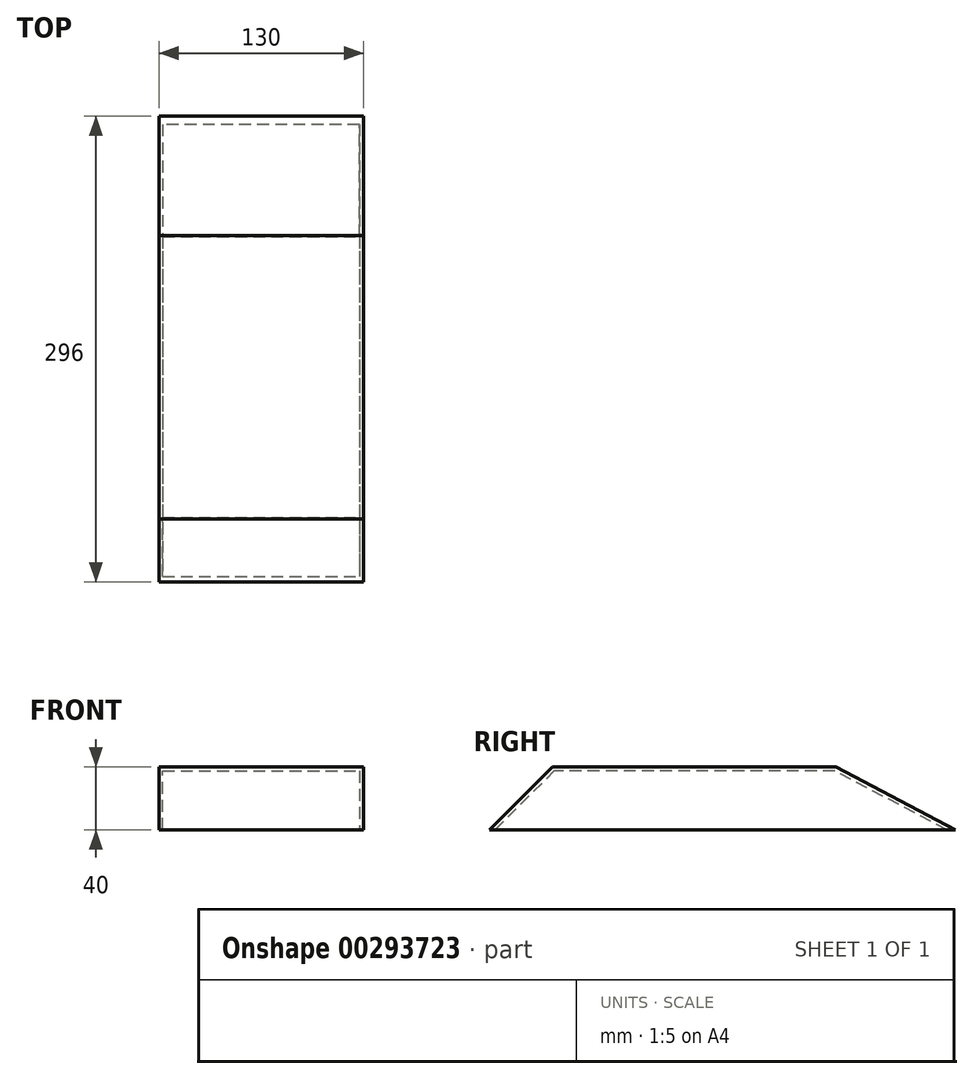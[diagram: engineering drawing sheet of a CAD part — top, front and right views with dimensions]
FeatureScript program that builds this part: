
annotation { "Feature Type Name" : "Feature", "Feature Type Description" : "" }
export const myFeature = defineFeature(function(context is Context, id is Id, definition is map)
    precondition{}
    {
        {
            var Q0;
            Q0=qCreatedBy(makeId("Top.planeOp"),FACE);
            var sketch = newSketch(context, id + "F0", { "sketchPlane" : qUnion([Q0])});
            skLineSegment(sketch, "E0.bottom", {"start": v(-65, 148) * mm, "end": v(65, 148) * mm});
            skLineSegment(sketch, "E0.top", {"start": v(-65, -148) * mm, "end": v(65, -148) * mm});
            skLineSegment(sketch, "E0.left", {"start": v(-65, 148) * mm, "end": v(-65, -148) * mm});
            skLineSegment(sketch, "E0.right", {"start": v(65, 148) * mm, "end": v(65, -148) * mm});
            skPoint(sketch, "E0.middle", {"position": v(0, 0) * mm});
            skSolve(sketch);
        }
        {
            var Q0;
            Q0 = qSketchRegion(id + "F0", true);
            extrude(context, id + "F1", {"entities" : qUnion([Q0]), "endBound" : BoundingType.SYMMETRIC, "depth" : 40 * mm});
        }
        {
            var Q0;
            Q0=makeQuery(id+"F1.opExtrude","CAP_EDGE",EDGE,{"disambiguationData":[OSD([sQuery(id+"F0.wireOp",EDGE,"E0.bottom")])],"isStart":false});
            chamfer(context, id + "F2", {"entities" : qUnion([Q0]), "chamferType" : ChamferType.TWO_OFFSETS, "width1" : 40 * mm, "oppositeDirection" : false, "width2" : 76 * mm, "tangentPropagation" : true});
        }
        {
            var Q0;
            Q0=makeQuery(id+"F1.opExtrude","CAP_EDGE",EDGE,{"disambiguationData":[OSD([sQuery(id+"F0.wireOp",EDGE,"E0.top")])],"isStart":false});
            chamfer(context, id + "F3", {"entities" : qUnion([Q0]), "chamferType" : ChamferType.TWO_OFFSETS, "width1" : 40 * mm, "oppositeDirection" : false, "width2" : 40 * mm, "tangentPropagation" : true});
        }
        {
            var Q0;
            Q0=makeQuery(id+"F1.opExtrude","CAP_FACE",FACE,{"disambiguationData":[OSD([sQuery(id+"F0.wireOp",EDGE,"E0.bottom"),sQuery(id+"F0.wireOp",EDGE,"E0.top"),sQuery(id+"F0.wireOp",EDGE,"E0.left"),sQuery(id+"F0.wireOp",EDGE,"E0.right")])],"isStart":true});
            shell(context, id + "F4", {"entities" : qUnion([Q0]), "thickness" : 2.5 * mm});
        }
    });
